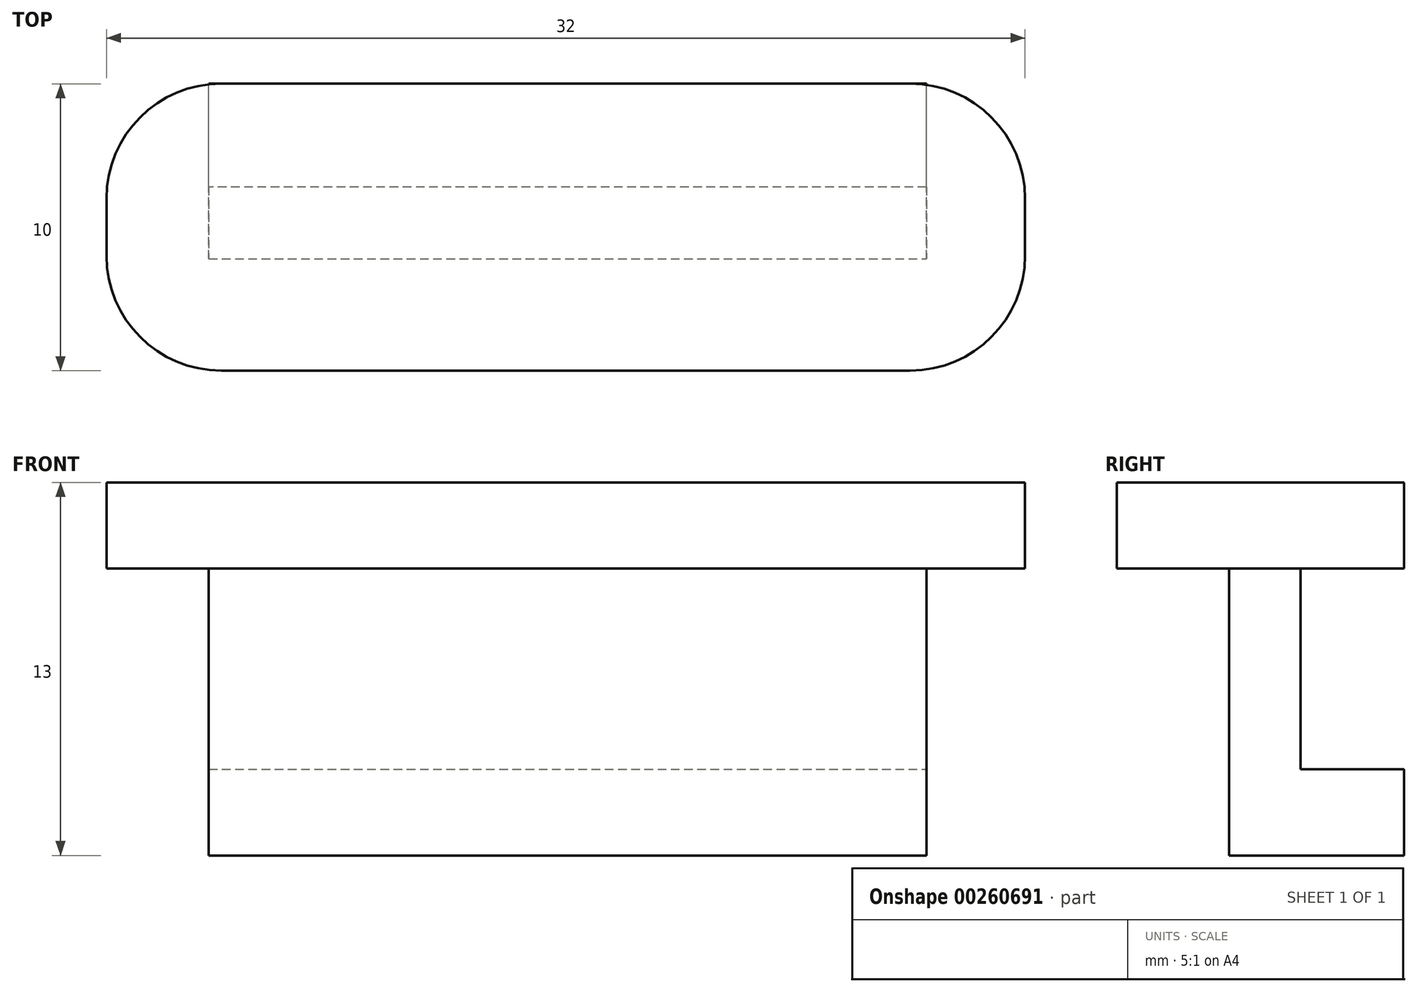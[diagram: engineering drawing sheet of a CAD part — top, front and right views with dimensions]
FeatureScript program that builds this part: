
annotation { "Feature Type Name" : "Feature", "Feature Type Description" : "" }
export const myFeature = defineFeature(function(context is Context, id is Id, definition is map)
    precondition{}
    {
        {
            var Q0;
            Q0=qCreatedBy(makeId("Top.planeOp"),FACE);
            var sketch = newSketch(context, id + "F0", { "sketchPlane" : qUnion([Q0])});
            skLineSegment(sketch, "E0.bottom", {"start": v(-11.9, 1.17) * mm, "end": v(13.1, 1.17) * mm});
            skLineSegment(sketch, "E0.top", {"start": v(-11.9, -1.33) * mm, "end": v(13.1, -1.33) * mm});
            skLineSegment(sketch, "E0.left", {"start": v(-11.9, 1.17) * mm, "end": v(-11.9, -1.33) * mm});
            skLineSegment(sketch, "E0.right", {"start": v(13.1, 1.17) * mm, "end": v(13.1, -1.33) * mm});
            skLineSegment(sketch, "E1.bottom", {"start": v(-15.47, 4.77) * mm, "end": v(16.53, 4.77) * mm});
            skLineSegment(sketch, "E1.top", {"start": v(-15.47, -5.23) * mm, "end": v(16.53, -5.23) * mm});
            skLineSegment(sketch, "E1.left", {"start": v(-15.47, 4.77) * mm, "end": v(-15.47, -5.23) * mm});
            skLineSegment(sketch, "E1.right", {"start": v(16.53, 4.77) * mm, "end": v(16.53, -5.23) * mm});
            skLineSegment(sketch, "E2", {"start": v(-11.9, 1.17) * mm, "end": v(-11.9, 31.22) * mm});
            skLineSegment(sketch, "E3", {"start": v(13.1, 1.17) * mm, "end": v(13.1, 31.78) * mm});
            skArc(sketch, "E4", {"start": v(-11.9, 31.22) * mm, "mid": v(0.31, 43.72) * mm, "end": v(13.1, 31.78) * mm});
            skCircle(sketch, "E5", {"center": v(0.6, 31.22) * mm, "radius": 7.56 * mm});
            skSolve(sketch);
        }
        {
            var Q0;
            {var subQ0=sQuery(id+"F0.wireOp",EDGE,"E4");Q0=makeQuery(id+"F0.imprint","IMPRINT",FACE,{"disambiguationData":[TD([[makeQuery(id+"F0.imprint","IMPRINT",EDGE,{"derivedFrom":subQ0}),-1.0]])]});}
            var Q1;
            {var subQ0=sQuery(id+"F0.wireOp",EDGE,"E0.bottom");Q1=makeQuery(id+"F0.imprint","IMPRINT",FACE,{"disambiguationData":[TD([[makeQuery(id+"F0.imprint","IMPRINT",EDGE,{"derivedFrom":subQ0}),1.0]])]});}
            var Q2;
            Q2=makeQuery(id+"F0.imprint","IMPRINT",FACE,{"disambiguationData":[TD([[makeQuery(id+"F0.imprint","IMPRINT",EDGE,{"derivedFrom":sQuery(id+"F0.wireOp",EDGE,"E0.bottom")}),-1.0]])]});
            extrude(context, id + "F1", {"entities" : qUnion([Q0, Q1, Q2]), "depth" : 3 * mm});
        }
        {
            var Q0;
            Q0=makeQuery(id+"F0.imprint","IMPRINT",FACE,{"disambiguationData":[TD([[makeQuery(id+"F0.imprint","IMPRINT",EDGE,{"derivedFrom":sQuery(id+"F0.wireOp",EDGE,"E0.bottom")}),-1.0]])]});
            extrude(context, id + "F2", {"entities" : qUnion([Q0]), "operationType" : NewBodyOperationType.ADD, "depth" : 10 * mm});
        }
        {
            var Q0;
            {var subQ0=sQuery(id+"F0.wireOp",EDGE,"E0.bottom");Q0=makeQuery(id+"F0.imprint","IMPRINT",FACE,{"disambiguationData":[TD([[makeQuery(id+"F0.imprint","IMPRINT",EDGE,{"derivedFrom":subQ0}),1.0]])]});}
            var Q1;
            Q1=makeQuery(id+"F0.imprint","IMPRINT",FACE,{"disambiguationData":[TD([[makeQuery(id+"F0.imprint","IMPRINT",EDGE,{"derivedFrom":sQuery(id+"F0.wireOp",EDGE,"E0.top")}),-1.0]])]});
            var Q2;
            Q2=makeQuery(id+"F0.imprint","IMPRINT",FACE,{"disambiguationData":[TD([[makeQuery(id+"F0.imprint","IMPRINT",EDGE,{"derivedFrom":sQuery(id+"F0.wireOp",EDGE,"E0.bottom")}),-1.0]])]});
            extrude(context, id + "F3", {"entities" : qUnion([Q0, Q1, Q2]), "operationType" : NewBodyOperationType.ADD, "depth" : 13 * mm, "hasSecondDirection" : true, "secondDirectionOppositeDirection" : false, "secondDirectionDepth" : 10 * mm});
        }
        {
            var Q0;
            Q0=makeQuery(id+"F3.opExtrude","SWEPT_EDGE",EDGE,{"disambiguationData":[OSD([sQuery(id+"F0.wireOp",EDGE,"E1.top"),sQuery(id+"F0.wireOp",EDGE,"E1.right")])]});
            var Q1;
            Q1=makeQuery(id+"F3.opExtrude","SWEPT_EDGE",EDGE,{"disambiguationData":[OSD([sQuery(id+"F0.wireOp",EDGE,"E1.bottom"),sQuery(id+"F0.wireOp",EDGE,"E1.right")])]});
            var Q2;
            Q2=makeQuery(id+"F3.opExtrude","SWEPT_EDGE",EDGE,{"disambiguationData":[OSD([sQuery(id+"F0.wireOp",EDGE,"E1.top"),sQuery(id+"F0.wireOp",EDGE,"E1.left")])]});
            var Q3;
            Q3=makeQuery(id+"F3.opExtrude","SWEPT_EDGE",EDGE,{"disambiguationData":[OSD([sQuery(id+"F0.wireOp",EDGE,"E1.bottom"),sQuery(id+"F0.wireOp",EDGE,"E1.left")])]});
            fillet(context, id + "F4", {"entities" : qUnion([Q0, Q1, Q2, Q3]), "radius" : 4 * mm, "tangentPropagation" : true, "allowEdgeOverflow" : false});
        }
    });
